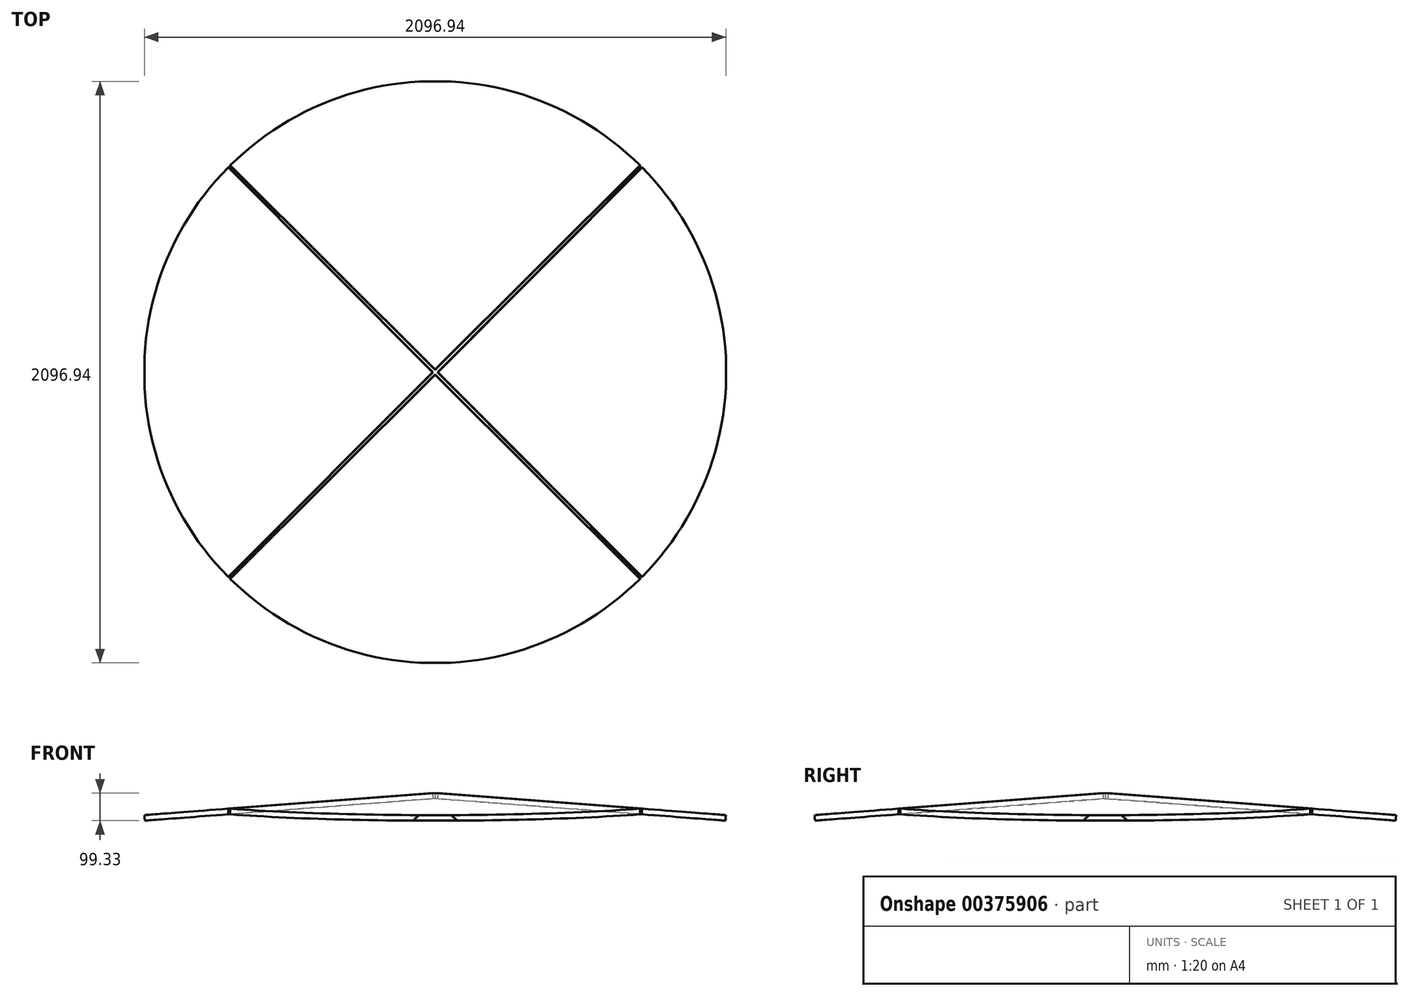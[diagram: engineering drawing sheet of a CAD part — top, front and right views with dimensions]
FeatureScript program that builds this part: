
annotation { "Feature Type Name" : "Feature", "Feature Type Description" : "" }
export const myFeature = defineFeature(function(context is Context, id is Id, definition is map)
    precondition{}
    {
        {
            var Q0;
            Q0=qCreatedBy(makeId("Top.planeOp"),FACE);
            var sketch = newSketch(context, id + "F0", { "sketchPlane" : qUnion([Q0])});
            skCircle(sketch, "E0", {"center": v(0, 0) * mm, "radius": 1050 * mm});
            skSolve(sketch);
        }
        {
            var Q0;
            Q0 = qSketchRegion(id + "F0", true);
            extrude(context, id + "F1", {"entities" : qUnion([Q0]), "depth" : 100 * mm});
        }
        {
            var Q0;
            Q0=qCreatedBy(makeId("Front.planeOp"),FACE);
            var sketch = newSketch(context, id + "F2", { "sketchPlane" : qUnion([Q0])});
            skLineSegment(sketch, "E1", {"start": v(0, 0) * mm, "end": v(0, 80) * mm});
            skLineSegment(sketch, "E2", {"start": v(1060, -20) * mm, "end": v(0, -20) * mm});
            skLineSegment(sketch, "E3", {"start": v(0, -20) * mm, "end": v(0, 0) * mm});
            skLineSegment(sketch, "E4", {"start": v(0, 80) * mm, "end": v(1046.95, 0) * mm});
            skLineSegment(sketch, "E5", {"start": v(0, 100.06) * mm, "end": v(0, 120.06) * mm});
            skLineSegment(sketch, "E6", {"start": v(0, 120.06) * mm, "end": v(1060, 120.06) * mm});
            skLineSegment(sketch, "E7", {"start": v(1060, 120.06) * mm, "end": v(1060, -20) * mm});
            skLineSegment(sketch, "E8", {"start": v(0, 100.06) * mm, "end": v(1048.47, 19.94) * mm});
            skLineSegment(sketch, "E9", {"start": v(1048.47, 19.94) * mm, "end": v(1046.95, 0) * mm});
            skSolve(sketch);
        }
        {
            var Q0;
            Q0=qCreatedBy(makeId("Front.planeOp"),FACE);
            var sketch = newSketch(context, id + "F3", { "sketchPlane" : qUnion([Q0])});
            skLineSegment(sketch, "E10", {"start": v(0, -250) * mm, "end": v(0, 250) * mm, "construction": true});
            skSolve(sketch);
        }
        {
            var Q0;
            Q0 = qSketchRegion(id + "F2", true);
            extrude(context, id + "F4", {"entities" : qUnion([Q0]), "operationType" : NewBodyOperationType.REMOVE, "endBound" : BoundingType.SYMMETRIC, "depth" : 2200 * mm});
        }
        {
            var Q0;
            Q0=makeQuery(id+"F4.boolean.opBoolean","COPY",FACE,{"derivedFrom":makeQuery(id+"F4.opExtrude","SWEPT_FACE",FACE,{"disambiguationData":[OSD([sQuery(id+"F2.wireOp",EDGE,"E8")])]})});
            cPlane(context, id + "F5", {"entities" : qUnion([Q0]), "cplaneType" : CPlaneType.OFFSET, "offset" : 25 * mm, "width" : 150 * mm, "height" : 150 * mm});
        }
        {
            var Q0;
            Q0=qCreatedBy(id+"F5.planeOp",FACE);
            var sketch = newSketch(context, id + "F6", { "sketchPlane" : qUnion([Q0])});
            skLineSegment(sketch, "E11", {"start": v(1102, 1100) * mm, "end": v(-1198, 1100) * mm});
            skLineSegment(sketch, "E12", {"start": v(-1198, 1100) * mm, "end": v(-1198, -1100) * mm});
            skLineSegment(sketch, "E13", {"start": v(-1198, -1100) * mm, "end": v(1102, -1100) * mm});
            skLineSegment(sketch, "E14", {"start": v(1102, -1100) * mm, "end": v(2, 0) * mm});
            skLineSegment(sketch, "E15", {"start": v(0, 0) * mm, "end": v(2, 0) * mm, "construction": true});
            skLineSegment(sketch, "E16", {"start": v(2, 0) * mm, "end": v(1102, 1100) * mm});
            skSolve(sketch);
        }
        {
            var Q0;
            Q0 = qSketchRegion(id + "F6", true);
            extrude(context, id + "F7", {"entities" : qUnion([Q0]), "operationType" : NewBodyOperationType.REMOVE, "endBound" : BoundingType.SYMMETRIC, "depth" : 500 * mm});
        }
        {
            var Q0;
            Q0=makeQuery(id+"F1.opExtrude","SWEPT_BODY",BODY,{"disambiguationData":[OSD([sQuery(id+"F0.wireOp",EDGE,"E0")])]});
            var Q1;
            Q1=sQuery(id+"F3.wireOp",EDGE,"E10");
            circularPattern(context, id + "F8", {"entities" : qUnion([Q0]), "axis" : qUnion([Q1]), "angle" : 360 * degree, "instanceCount" : 4, "equalSpace" : true});
        }
    });
